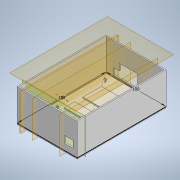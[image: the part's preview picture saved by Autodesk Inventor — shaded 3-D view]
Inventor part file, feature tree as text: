
AUTODESK INVENTOR PART (.ipt)
format: ipt  version: 2021 (Build 250183000, 183)  size: 352,768 bytes
history: native  units: in
note: dims shown in document units (in); Inventor stores cm internally (conversion verified against a paired STEP export)
features: sketch x20, reference x16, extrude x13, plane x6, other x4, revolve x2, mirror x1, chamfer x1
ambient origin geometry x8: Origin, YZ Plane, XZ Plane, XY Plane, X Axis, Y Axis, Z Axis, Center Point
bodies: Solid1 (feature_tree)
feature tree (63):
  sketch  "Sketch1"  dims[d0=3.937in d1=5.9055in]
  extrude  "Extrusion1"  Depth=5.9055in
  extrude  "Extrusion2"  Depth=2.1654in TaperAngle=0.0deg
  sketch  "Sketch2"  dims[d5=0.0787in d6=0.0in d7=-1.5748in]
  plane  "Work Plane1"
  extrude  "Extrusion3"  [1 undecoded]
  sketch  "Sketch7"  dims[d19=0.0787in d20=0.0in d21=2.8346in]
  plane  "Work Plane2"
  revolve  "Revolution2"  [1 undecoded]
  plane  "Work Plane3"
  extrude  "Extrusion4"  Depth=0.7087in
  sketch  "Sketch Driven Pattern1"  dims[d2=0.0787in d3=2.1654in d4=0.0in]
  extrude  "Extrusion5"  Depth=2.8346in
  plane  "Work Plane4"
  extrude  "Extrusion6"  Depth=0.1102in
  extrude  "Extrusion7"  Depth=0.1378in
  extrude  "Extrusion8"  Depth=0.0689in
  mirror  "Mirror1"
  plane  "Work Plane5"
  extrude  "Extrusion9"  Depth=3.0in
  extrude  "Extrusion10"  Depth=0.1946in
  extrude  "Extrusion11"  Depth=0.0787in TaperAngle=0.0deg
  chamfer  "Chamfer1"  Distance=0.0787in
  extrude  "Extrusion12"  Depth=1.1811in
  sketch  "Sketch22"  dims[d45=0.0906in d46=0.3819in]
  plane  "Work Plane6"
  revolve  "Revolution3"  [1 undecoded]
  extrude  "Extrusion13"  Depth=0.3819in
  sketch  "Sketch Driven Pattern2"  dims[d15=1.378in d16=1.2598in]
  sketch  "Sketch27"  dims[d50=0.4409in d51=0.3236in d52=0.5933in d53=0.0in d54=0.4724in d55=0.5933in d56=0.0in d57=0.1575in d58=0.0787in d59=45.0deg d63=0.3937in d64=0.0906in d65=0.4606in d66=0.9843in d67=0.5933in d68=0.0in d69=0.0866in d70=0.4409in d71=0.3236in d72=0.5933in d73=0.0in d74=0.4724in d75=0.5933in d76=0.0in d77=0.2756in d78=0.5906in d79=0.0787in d80=0.0in d81=90.0deg d82=0.0276in d83=0.0394in d84=0.0in]
  sketch  "Sketch6"  dims[d17=1.0236in d18=0.7087in]
  reference  "Reference1"
  reference  "Reference2"
  reference  "Reference3"
  reference  "Reference4"
  sketch  "Sketch8"  dims[d22=0.7087in d23=0.1102in]
  sketch  "Sketch9"  dims[d26=0.1102in d27=0.1378in]
  sketch  "Sketch10"  dims[d28=0.1575in d29=0.0689in]
  reference  "Reference5"
  reference  "Reference6"
  reference  "Reference7"
  reference  "Reference8"
  reference  "Reference9"
  reference  "Reference10"
  sketch  "Sketch11"  dims[d30=90.0deg d31=3.0in]
  sketch  "Sketch13"  dims[d32=0.0394in d33=0.1946in]
  sketch  "Sketch15"  dims[d34=0.0299in d35=0.0787in d36=0.0in]
  sketch  "Sketch18"  dims[d37=0.0157in]
  sketch  "Sketch19"  dims[d38=0.0157in d39=0.0787in d40=0.0in]
  sketch  "Sketch20"  dims[d41=0.9055in d42=1.1811in]
  sketch  "Sketch21"  dims[d43=0.4606in d44=0.9843in]
  reference  "Reference11"
  reference  "Reference12"
  reference  "Reference13"
  reference  "Reference14"
  reference  "Reference15"
  reference  "Reference16"
  sketch  "Sketch25"  dims[d47=0.5933in d48=0.0in]
  sketch  "Sketch26"  dims[d49=0.0866in]
  other  "Chestbox_with_electronical_devices.iam"
  other  "ArduinoMega_STEP_AP203:1"
  other  "TCA9548A Adfruit with Header:1"
  other  "Part57"
note: 3 required parameter values undecoded (feature->parameter linkage not recoverable at this tier; creation-order binding heuristic only, values carry confidence <= 0.55)